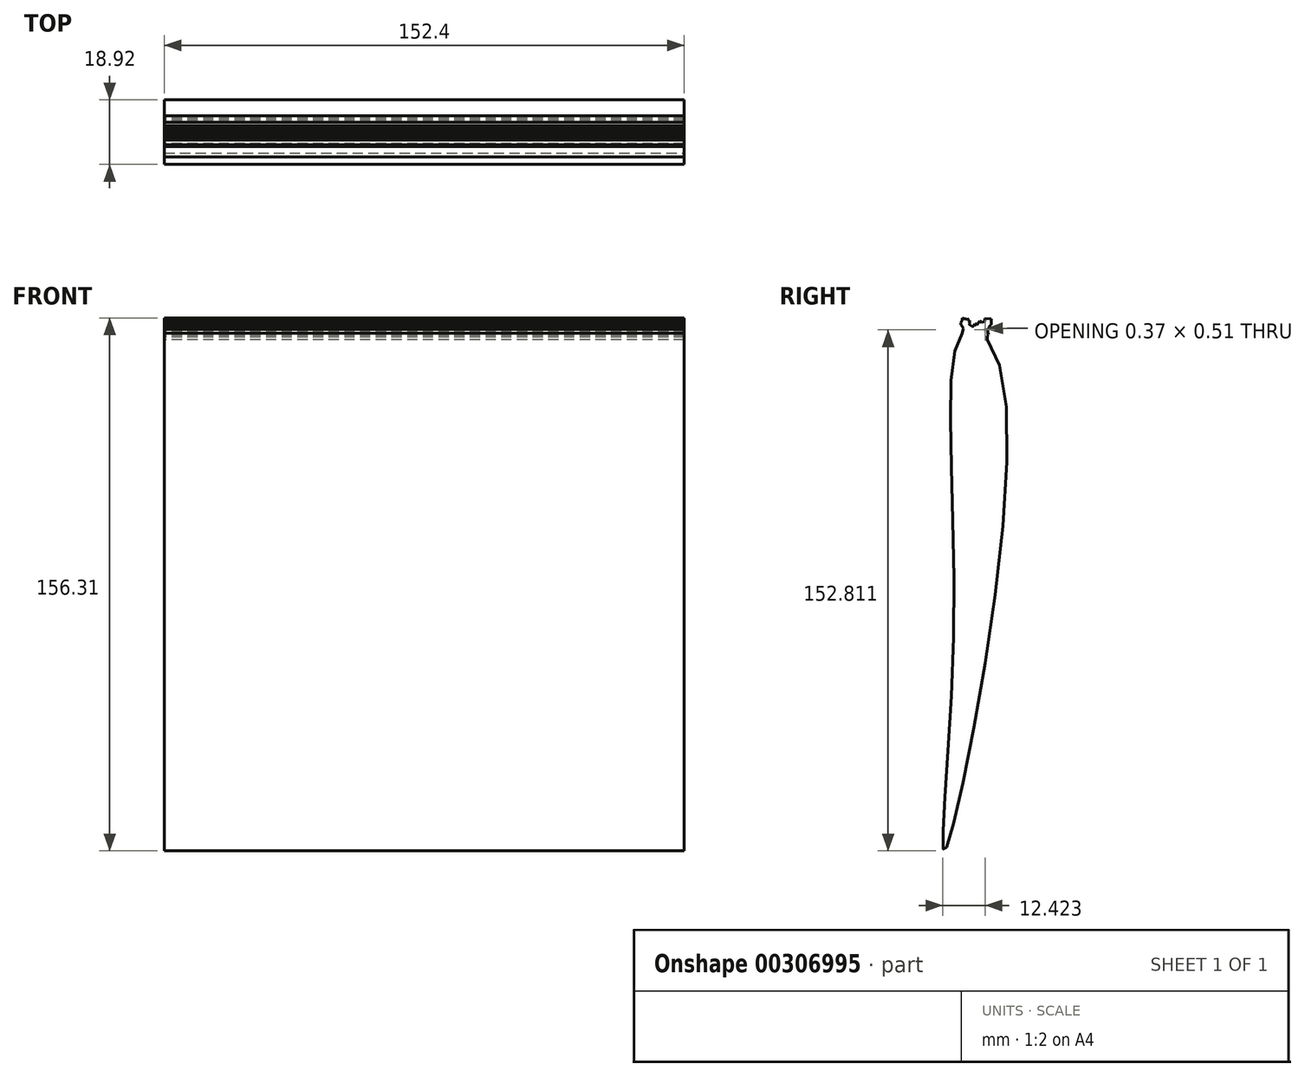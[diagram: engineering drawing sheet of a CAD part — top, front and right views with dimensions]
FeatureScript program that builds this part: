
annotation { "Feature Type Name" : "Feature", "Feature Type Description" : "" }
export const myFeature = defineFeature(function(context is Context, id is Id, definition is map)
    precondition{}
    {
        {
            var Q0;
            Q0=qCreatedBy(makeId("Right.planeOp"),FACE);
            var sketch = newSketch(context, id + "F0", { "sketchPlane" : qUnion([Q0])});
            skFitSpline(sketch, "E0", {"points": [v(3.27, 75.24) * mm, v(14.59, 61.8) * mm, v(-2.03, -76.46) * mm, v(0.33, -8.8) * mm, v(3.27, 75.24) * mm]});
            skLineSegment(sketch, "E1", {"start": v(7.38, 75.47) * mm, "end": v(9.7, 78.26) * mm});
            skLineSegment(sketch, "E2", {"start": v(9.7, 78.26) * mm, "end": v(10.74, 77.5) * mm});
            skLineSegment(sketch, "E3", {"start": v(10.74, 77.5) * mm, "end": v(8.64, 74.6) * mm});
            skLineSegment(sketch, "E4", {"start": v(8.64, 74.6) * mm, "end": v(7.38, 75.47) * mm});
            skLineSegment(sketch, "E5", {"start": v(9.7, 78.26) * mm, "end": v(10.26, 79.03) * mm});
            skPoint(sketch, "E5.endSnap0", {"position": v(10.22, 77.88) * mm});
            skLineSegment(sketch, "E6", {"start": v(10.26, 79.03) * mm, "end": v(11.26, 78.2) * mm});
            skLineSegment(sketch, "E7", {"start": v(11.26, 78.2) * mm, "end": v(10.74, 77.5) * mm});
            skLineSegment(sketch, "E8", {"start": v(4.91, 75.99) * mm, "end": v(3.97, 78.46) * mm});
            skLineSegment(sketch, "E9", {"start": v(3.97, 78.46) * mm, "end": v(2.76, 78) * mm});
            skLineSegment(sketch, "E10", {"start": v(2.76, 78) * mm, "end": v(3.7, 75.55) * mm});
            skLineSegment(sketch, "E11", {"start": v(3.7, 75.55) * mm, "end": v(4.91, 75.99) * mm});
            skLineSegment(sketch, "E12", {"start": v(9.27, 74.1) * mm, "end": v(9.32, 75.53) * mm});
            skLineSegment(sketch, "E13", {"start": v(9.32, 75.53) * mm, "end": v(9.69, 76.05) * mm});
            skLineSegment(sketch, "E14", {"start": v(9.69, 76.05) * mm, "end": v(9.68, 75.78) * mm});
            skPoint(sketch, "E14.endSnap0", {"position": v(9.5, 75.8) * mm});
            skLineSegment(sketch, "E15", {"start": v(9.68, 75.78) * mm, "end": v(9.32, 75.53) * mm});
            skLineSegment(sketch, "E16", {"start": v(9.3, 74.82) * mm, "end": v(9.9, 75.65) * mm});
            skLineSegment(sketch, "E17", {"start": v(9.9, 75.65) * mm, "end": v(9.92, 76.36) * mm});
            skLineSegment(sketch, "E18", {"start": v(9.92, 76.36) * mm, "end": v(10.37, 76.03) * mm});
            skLineSegment(sketch, "E19", {"start": v(10.37, 76.03) * mm, "end": v(9.9, 75.65) * mm});
            skLineSegment(sketch, "E20", {"start": v(10.45, 77.1) * mm, "end": v(11.3, 77.07) * mm});
            skLineSegment(sketch, "E21", {"start": v(11.3, 77.07) * mm, "end": v(10.74, 77.5) * mm});
            skLineSegment(sketch, "E22", {"start": v(11.26, 78.2) * mm, "end": v(11.31, 77.48) * mm});
            skLineSegment(sketch, "E23", {"start": v(11.31, 77.48) * mm, "end": v(10.71, 76.65) * mm});
            skLineSegment(sketch, "E24", {"start": v(10.71, 76.65) * mm, "end": v(9.92, 76.36) * mm});
            skLineSegment(sketch, "E25", {"start": v(10.71, 76.65) * mm, "end": v(10.7, 76.33) * mm});
            skLineSegment(sketch, "E26", {"start": v(10.7, 76.33) * mm, "end": v(10.37, 76.03) * mm});
            skLineSegment(sketch, "E27", {"start": v(11.31, 77.48) * mm, "end": v(10.74, 77.5) * mm});
            skLineSegment(sketch, "E28", {"start": v(10.37, 76.03) * mm, "end": v(10.34, 75.05) * mm});
            skLineSegment(sketch, "E29", {"start": v(10.34, 75.05) * mm, "end": v(9.3, 74.82) * mm});
            skLineSegment(sketch, "E30", {"start": v(11.26, 78.2) * mm, "end": v(11.28, 79) * mm});
            skLineSegment(sketch, "E31", {"start": v(11.28, 79) * mm, "end": v(10.91, 78.49) * mm});
            skLineSegment(sketch, "E32", {"start": v(10.91, 78.49) * mm, "end": v(11.28, 79) * mm});
            skLineSegment(sketch, "E33", {"start": v(11.28, 79) * mm, "end": v(10.26, 79.03) * mm});
            skLineSegment(sketch, "E34", {"start": v(10.26, 79.03) * mm, "end": v(9.44, 79.06) * mm});
            skLineSegment(sketch, "E35", {"start": v(9.44, 79.06) * mm, "end": v(9.41, 78.27) * mm});
            skLineSegment(sketch, "E36", {"start": v(9.41, 78.27) * mm, "end": v(8.46, 77.94) * mm});
            skLineSegment(sketch, "E37", {"start": v(8.46, 77.94) * mm, "end": v(7.94, 78.32) * mm});
            skLineSegment(sketch, "E38", {"start": v(7.94, 78.32) * mm, "end": v(7.9, 77.18) * mm});
            skLineSegment(sketch, "E39", {"start": v(7.9, 77.18) * mm, "end": v(7.88, 76.75) * mm});
            skLineSegment(sketch, "E40", {"start": v(7.88, 76.75) * mm, "end": v(7.16, 76.6) * mm});
            skLineSegment(sketch, "E41", {"start": v(7.16, 76.6) * mm, "end": v(7.12, 75.7) * mm});
            skLineSegment(sketch, "E42", {"start": v(7.12, 75.7) * mm, "end": v(7.38, 75.47) * mm});
            skLineSegment(sketch, "E43", {"start": v(7.94, 78.32) * mm, "end": v(7.13, 77.21) * mm});
            skLineSegment(sketch, "E44", {"start": v(7.13, 77.21) * mm, "end": v(6.53, 77.64) * mm});
            skLineSegment(sketch, "E45", {"start": v(6.53, 77.64) * mm, "end": v(6.27, 76.8) * mm});
            skLineSegment(sketch, "E46", {"start": v(6.27, 76.8) * mm, "end": v(5.55, 76.83) * mm});
            skLineSegment(sketch, "E47", {"start": v(5.55, 76.83) * mm, "end": v(5.08, 76.18) * mm});
            skLineSegment(sketch, "E48", {"start": v(5.55, 76.83) * mm, "end": v(4.92, 77.29) * mm});
            skLineSegment(sketch, "E49", {"start": v(4.92, 77.29) * mm, "end": v(4.62, 76.87) * mm});
            skLineSegment(sketch, "E50", {"start": v(4.62, 76.87) * mm, "end": v(4.64, 77.7) * mm});
            skLineSegment(sketch, "E51", {"start": v(4.64, 77.7) * mm, "end": v(4.12, 78.09) * mm});
            skLineSegment(sketch, "E52", {"start": v(4.12, 78.09) * mm, "end": v(3.97, 78.46) * mm});
            skLineSegment(sketch, "E53", {"start": v(4.64, 77.7) * mm, "end": v(4.67, 78.43) * mm});
            skLineSegment(sketch, "E54", {"start": v(4.67, 78.43) * mm, "end": v(4.12, 78.09) * mm});
            skLineSegment(sketch, "E55", {"start": v(4.67, 78.43) * mm, "end": v(5.2, 78.05) * mm});
            skLineSegment(sketch, "E56", {"start": v(5.2, 78.05) * mm, "end": v(4.64, 77.7) * mm});
            skLineSegment(sketch, "E57", {"start": v(4.67, 78.43) * mm, "end": v(4.36, 79.24) * mm});
            skLineSegment(sketch, "E58", {"start": v(4.36, 79.24) * mm, "end": v(3.97, 78.46) * mm});
            skLineSegment(sketch, "E59", {"start": v(3.97, 78.46) * mm, "end": v(3.39, 78.88) * mm});
            skPoint(sketch, "E59.endSnap0", {"position": v(3.37, 78.23) * mm});
            skLineSegment(sketch, "E60", {"start": v(3.39, 78.88) * mm, "end": v(2.76, 78) * mm});
            skLineSegment(sketch, "E61", {"start": v(2.76, 78) * mm, "end": v(2.8, 79.3) * mm});
            skLineSegment(sketch, "E62", {"start": v(2.8, 79.3) * mm, "end": v(4.17, 78.85) * mm});
            skLineSegment(sketch, "E63", {"start": v(4.17, 78.85) * mm, "end": v(4.36, 79.24) * mm});
            skLineSegment(sketch, "E64", {"start": v(2.78, 78.5) * mm, "end": v(2.26, 77.8) * mm});
            skLineSegment(sketch, "E65", {"start": v(2.26, 77.8) * mm, "end": v(3.3, 76.6) * mm});
            skLineSegment(sketch, "E66", {"start": v(3.3, 76.6) * mm, "end": v(2.62, 76.94) * mm});
            skLineSegment(sketch, "E67", {"start": v(2.62, 76.94) * mm, "end": v(2.45, 77.37) * mm});
            skLineSegment(sketch, "E68", {"start": v(2.45, 77.37) * mm, "end": v(2.26, 77.8) * mm});
            skLineSegment(sketch, "E69", {"start": v(3.7, 75.55) * mm, "end": v(3.27, 75.24) * mm});
            skLineSegment(sketch, "E70", {"start": v(3.27, 75.24) * mm, "end": v(3.02, 75.89) * mm});
            skLineSegment(sketch, "E71", {"start": v(3.02, 75.89) * mm, "end": v(3.38, 76.5) * mm});
            skLineSegment(sketch, "E72", {"start": v(3.38, 76.5) * mm, "end": v(2.62, 76.94) * mm});
            skLineSegment(sketch, "E73", {"start": v(2.62, 76.94) * mm, "end": v(3.2, 76.2) * mm});
            skLineSegment(sketch, "E74", {"start": v(10.34, 75.05) * mm, "end": v(10.5, 74.37) * mm});
            skLineSegment(sketch, "E75", {"start": v(10.5, 74.37) * mm, "end": v(10, 74.2) * mm});
            skLineSegment(sketch, "E76", {"start": v(10, 74.2) * mm, "end": v(10.2, 73.6) * mm});
            skLineSegment(sketch, "E77", {"start": v(10.2, 73.6) * mm, "end": v(10.18, 72.93) * mm});
            skLineSegment(sketch, "E78", {"start": v(10.18, 72.93) * mm, "end": v(9.27, 74.1) * mm});
            skLineSegment(sketch, "E79", {"start": v(3.02, 75.89) * mm, "end": v(2.75, 74.74) * mm});
            skLineSegment(sketch, "E80", {"start": v(2.75, 74.74) * mm, "end": v(3.27, 75.24) * mm});
            skLineSegment(sketch, "E81", {"start": v(4.64, 77.7) * mm, "end": v(4.92, 77.29) * mm});
            skLineSegment(sketch, "E82.0", {"start": v(3.02, 75.89) * mm, "end": v(9.9, 75.65) * mm, "construction": true});
            skLineSegment(sketch, "E83.0", {"start": v(2.45, 77.37) * mm, "end": v(11.3, 77.07) * mm, "construction": true});
            skLineSegment(sketch, "E84.0", {"start": v(2.62, 76.94) * mm, "end": v(5.55, 76.83) * mm, "construction": true});
            skLineSegment(sketch, "E85.0", {"start": v(3.3, 76.6) * mm, "end": v(10.7, 76.33) * mm, "construction": true});
            skLineSegment(sketch, "E86.0", {"start": v(2.26, 77.8) * mm, "end": v(11.31, 77.48) * mm, "construction": true});
            skLineSegment(sketch, "E87.0", {"start": v(2.8, 79.3) * mm, "end": v(11.28, 79) * mm, "construction": true});
            skLineSegment(sketch, "E88.0", {"start": v(2.78, 78.5) * mm, "end": v(11.26, 78.2) * mm, "construction": true});
            skLineSegment(sketch, "E89.0", {"start": v(4.12, 78.09) * mm, "end": v(10.22, 77.88) * mm, "construction": true});
            skLineSegment(sketch, "E90.0", {"start": v(9.5, 75.8) * mm, "end": v(9.68, 75.78) * mm, "construction": true});
            skLineSegment(sketch, "E91.0", {"start": v(7.13, 77.21) * mm, "end": v(7.9, 77.18) * mm, "construction": true});
            skLineSegment(sketch, "E92.0", {"start": v(7.88, 76.75) * mm, "end": v(10.71, 76.65) * mm, "construction": true});
            skLineSegment(sketch, "E93.0", {"start": v(3.3, 76.6) * mm, "end": v(3.39, 78.88) * mm, "construction": true});
            skLineSegment(sketch, "E94.0", {"start": v(10.71, 76.65) * mm, "end": v(10.74, 77.5) * mm, "construction": true});
            skLineSegment(sketch, "E95.0", {"start": v(2.76, 78) * mm, "end": v(2.78, 78.5) * mm, "construction": true});
            skLineSegment(sketch, "E96.0", {"start": v(10.22, 77.88) * mm, "end": v(10.26, 79.03) * mm, "construction": true});
            skLineSegment(sketch, "E97.0", {"start": v(9.3, 74.82) * mm, "end": v(9.44, 79.06) * mm, "construction": true});
            skLineSegment(sketch, "E98.0", {"start": v(11.3, 77.07) * mm, "end": v(11.31, 77.48) * mm, "construction": true});
            skSolve(sketch);
        }
        {
            var Q0;
            Q0=qSketchRegion(id+"F0",true);
            var Q1;
            Q1=makeQuery(id+"F0.imprint","IMPRINT",FACE,{"disambiguationData":[TD([[makeQuery(id+"F0.imprint","IMPRINT",EDGE,{"derivedFrom":sQuery(id+"F0.wireOp",EDGE,"E1")}),1.0]])]});
            var Q2;
            {var subQ3=sQuery(id+"F0.wireOp",EDGE,"E1");Q2=makeQuery(id+"F0.imprint","IMPRINT",FACE,{"disambiguationData":[TD([[makeQuery(id+"F0.imprint","IMPRINT",EDGE,{"derivedFrom":subQ3}),-1.0]])]});}
            var Q3;
            {var subQ0=sQuery(id+"F0.wireOp",EDGE,"E29");Q3=makeQuery(id+"F0.imprint","IMPRINT",FACE,{"disambiguationData":[TD([[makeQuery(id+"F0.imprint","IMPRINT",EDGE,{"derivedFrom":subQ0}),1.0]])]});}
            var Q4;
            {var subQ0=sQuery(id+"F0.wireOp",EDGE,"E78");var subQ1=sQuery(id+"F0.wireOp",EDGE,"E12");var subQ2=makeQuery(id+"F0.imprint","INTERSECT",VERTEX,{"derivedFrom":[subQ1,subQ0]});Q4=makeQuery(id+"F0.imprint","IMPRINT",FACE,{"disambiguationData":[TD([[makeQuery(id+"F0.imprint","IMPRINT",EDGE,{"disambiguationData":[TD([[subQ2,1.0]])],"derivedFrom":subQ0}),1.0]])]});}
            var Q5;
            {var subQ2=sQuery(id+"F0.wireOp",EDGE,"E8");Q5=makeQuery(id+"F0.imprint","IMPRINT",FACE,{"disambiguationData":[TD([[makeQuery(id+"F0.imprint","IMPRINT",EDGE,{"derivedFrom":subQ2}),-1.0]])]});}
            var Q6;
            {var subQ0=sQuery(id+"F0.wireOp",EDGE,"E11");Q6=makeQuery(id+"F0.imprint","IMPRINT",FACE,{"disambiguationData":[TD([[makeQuery(id+"F0.imprint","IMPRINT",EDGE,{"derivedFrom":subQ0}),1.0]])]});}
            var Q7;
            {var subQ0=sQuery(id+"F0.wireOp",EDGE,"E4");Q7=makeQuery(id+"F0.imprint","IMPRINT",FACE,{"disambiguationData":[TD([[makeQuery(id+"F0.imprint","IMPRINT",EDGE,{"derivedFrom":subQ0}),-1.0]])]});}
            var Q8;
            {var subQ0=sQuery(id+"F0.wireOp",EDGE,"E78");var subQ1=sQuery(id+"F0.wireOp",EDGE,"E0");var subQ3=makeQuery(id+"F0.imprint","INTERSECT",VERTEX,{"derivedFrom":[subQ1,subQ0]});Q8=makeQuery(id+"F0.imprint","IMPRINT",FACE,{"disambiguationData":[TD([[makeQuery(id+"F0.imprint","IMPRINT",EDGE,{"disambiguationData":[TD([[subQ3,-1.0]])],"derivedFrom":subQ1}),-1.0]])]});}
            var Q9;
            {var subQ6=sQuery(id+"F0.wireOp",EDGE,"E8");Q9=makeQuery(id+"F0.imprint","IMPRINT",FACE,{"disambiguationData":[TD([[makeQuery(id+"F0.imprint","IMPRINT",EDGE,{"derivedFrom":subQ6}),1.0]])]});}
            var Q10;
            Q10=makeQuery(id+"F0.imprint","IMPRINT",FACE,{"disambiguationData":[TD([[makeQuery(id+"F0.imprint","IMPRINT",EDGE,{"derivedFrom":sQuery(id+"F0.wireOp",EDGE,"E58")}),-1.0]])]});
            var Q11;
            {var subQ0=sQuery(id+"F0.wireOp",EDGE,"E69");Q11=makeQuery(id+"F0.imprint","IMPRINT",FACE,{"disambiguationData":[TD([[makeQuery(id+"F0.imprint","IMPRINT",EDGE,{"derivedFrom":subQ0}),-1.0]])]});}
            var Q12;
            {var subQ1=sQuery(id+"F0.wireOp",EDGE,"E70");Q12=makeQuery(id+"F0.imprint","IMPRINT",FACE,{"disambiguationData":[TD([[makeQuery(id+"F0.imprint","IMPRINT",EDGE,{"derivedFrom":subQ1}),1.0]])]});}
            var Q13;
            {var subQ0=sQuery(id+"F0.wireOp",EDGE,"E80");Q13=makeQuery(id+"F0.imprint","IMPRINT",FACE,{"disambiguationData":[TD([[makeQuery(id+"F0.imprint","IMPRINT",EDGE,{"derivedFrom":subQ0}),1.0]])]});}
            var Q14;
            {var subQ5=sQuery(id+"F0.wireOp",EDGE,"E64");Q14=makeQuery(id+"F0.imprint","IMPRINT",FACE,{"disambiguationData":[TD([[makeQuery(id+"F0.imprint","IMPRINT",EDGE,{"derivedFrom":subQ5}),1.0]])]});}
            var Q15;
            {var subQ1=sQuery(id+"F0.wireOp",EDGE,"E70");Q15=makeQuery(id+"F0.imprint","IMPRINT",FACE,{"disambiguationData":[TD([[makeQuery(id+"F0.imprint","IMPRINT",EDGE,{"derivedFrom":subQ1}),-1.0]])]});}
            var Q16;
            {var subQ0=sQuery(id+"F0.wireOp",EDGE,"E67");Q16=makeQuery(id+"F0.imprint","IMPRINT",FACE,{"disambiguationData":[TD([[makeQuery(id+"F0.imprint","IMPRINT",EDGE,{"derivedFrom":subQ0}),-1.0]])]});}
            var Q17;
            {var subQ0=sQuery(id+"F0.wireOp",EDGE,"E72");var subQ1=sQuery(id+"F0.wireOp",EDGE,"E10");var subQ2=makeQuery(id+"F0.imprint","INTERSECT",VERTEX,{"derivedFrom":[subQ1,subQ0]});Q17=makeQuery(id+"F0.imprint","IMPRINT",FACE,{"disambiguationData":[TD([[makeQuery(id+"F0.imprint","IMPRINT",EDGE,{"disambiguationData":[TD([[subQ2,-1.0]])],"derivedFrom":subQ1}),1.0]])]});}
            var Q18;
            Q18=makeQuery(id+"F0.imprint","IMPRINT",FACE,{"disambiguationData":[TD([[makeQuery(id+"F0.imprint","IMPRINT",EDGE,{"derivedFrom":sQuery(id+"F0.wireOp",EDGE,"E9")}),-1.0]])]});
            var Q19;
            Q19=makeQuery(id+"F0.imprint","IMPRINT",FACE,{"disambiguationData":[TD([[makeQuery(id+"F0.imprint","IMPRINT",EDGE,{"derivedFrom":sQuery(id+"F0.wireOp",EDGE,"E17")}),-1.0]])]});
            var Q20;
            {var subQ0=sQuery(id+"F0.wireOp",EDGE,"E65");var subQ1=sQuery(id+"F0.wireOp",EDGE,"E10");var subQ2=makeQuery(id+"F0.imprint","INTERSECT",VERTEX,{"derivedFrom":[subQ1,subQ0]});Q20=makeQuery(id+"F0.imprint","IMPRINT",FACE,{"disambiguationData":[TD([[makeQuery(id+"F0.imprint","IMPRINT",EDGE,{"disambiguationData":[TD([[subQ2,-1.0]])],"derivedFrom":subQ1}),1.0]])]});}
            var Q21;
            Q21=makeQuery(id+"F0.imprint","IMPRINT",FACE,{"disambiguationData":[TD([[makeQuery(id+"F0.imprint","IMPRINT",EDGE,{"derivedFrom":sQuery(id+"F0.wireOp",EDGE,"E18")}),1.0]])]});
            var Q22;
            Q22=makeQuery(id+"F0.imprint","IMPRINT",FACE,{"disambiguationData":[TD([[makeQuery(id+"F0.imprint","IMPRINT",EDGE,{"derivedFrom":sQuery(id+"F0.wireOp",EDGE,"E49")}),-1.0]])]});
            var Q23;
            {var subQ2=sQuery(id+"F0.wireOp",EDGE,"E32");Q23=makeQuery(id+"F0.imprint","IMPRINT",FACE,{"disambiguationData":[TD([[makeQuery(id+"F0.imprint","IMPRINT",EDGE,{"derivedFrom":subQ2}),1.0]])]});}
            var Q24;
            {var subQ0=sQuery(id+"F0.wireOp",EDGE,"E66");var subQ1=sQuery(id+"F0.wireOp",EDGE,"E10");var subQ2=makeQuery(id+"F0.imprint","INTERSECT",VERTEX,{"derivedFrom":[subQ1,subQ0]});Q24=makeQuery(id+"F0.imprint","IMPRINT",FACE,{"disambiguationData":[TD([[makeQuery(id+"F0.imprint","IMPRINT",EDGE,{"disambiguationData":[TD([[subQ2,-1.0]])],"derivedFrom":subQ1}),-1.0]])]});}
            var Q25;
            Q25=makeQuery(id+"F0.imprint","IMPRINT",FACE,{"disambiguationData":[TD([[makeQuery(id+"F0.imprint","IMPRINT",EDGE,{"derivedFrom":sQuery(id+"F0.wireOp",EDGE,"E2")}),1.0]])]});
            var Q26;
            {var subQ5=sQuery(id+"F0.wireOp",EDGE,"E73");Q26=makeQuery(id+"F0.imprint","IMPRINT",FACE,{"disambiguationData":[TD([[makeQuery(id+"F0.imprint","IMPRINT",EDGE,{"derivedFrom":subQ5}),1.0]])]});}
            var Q27;
            {var subQ1=sQuery(id+"F0.wireOp",EDGE,"E14");Q27=makeQuery(id+"F0.imprint","IMPRINT",FACE,{"disambiguationData":[TD([[makeQuery(id+"F0.imprint","IMPRINT",EDGE,{"derivedFrom":subQ1}),1.0]])]});}
            var Q28;
            Q28=makeQuery(id+"F0.imprint","IMPRINT",FACE,{"disambiguationData":[TD([[makeQuery(id+"F0.imprint","IMPRINT",EDGE,{"derivedFrom":sQuery(id+"F0.wireOp",EDGE,"E16")}),-1.0]])]});
            var Q29;
            {var subQ0=sQuery(id+"F0.wireOp",EDGE,"E24");Q29=makeQuery(id+"F0.imprint","IMPRINT",FACE,{"disambiguationData":[TD([[makeQuery(id+"F0.imprint","IMPRINT",EDGE,{"derivedFrom":subQ0}),-1.0]])]});}
            var Q30;
            Q30=makeQuery(id+"F0.imprint","IMPRINT",FACE,{"disambiguationData":[TD([[makeQuery(id+"F0.imprint","IMPRINT",EDGE,{"derivedFrom":sQuery(id+"F0.wireOp",EDGE,"E13")}),-1.0]])]});
            var Q31;
            {var subQ0=sQuery(id+"F0.wireOp",EDGE,"E21");var subQ1=sQuery(id+"F0.wireOp",EDGE,"E20");var subQ2=makeQuery(id+"F0.imprint","INTERSECT",VERTEX,{"derivedFrom":[subQ1,subQ0]});Q31=makeQuery(id+"F0.imprint","IMPRINT",FACE,{"disambiguationData":[TD([[makeQuery(id+"F0.imprint","IMPRINT",EDGE,{"disambiguationData":[TD([[subQ2,1.0]])],"derivedFrom":subQ1}),1.0]])]});}
            var Q32;
            Q32=makeQuery(id+"F0.imprint","IMPRINT",FACE,{"disambiguationData":[TD([[makeQuery(id+"F0.imprint","IMPRINT",EDGE,{"derivedFrom":sQuery(id+"F0.wireOp",EDGE,"E53")}),-1.0]])]});
            var Q33;
            {var subQ0=sQuery(id+"F0.wireOp",EDGE,"E30");Q33=makeQuery(id+"F0.imprint","IMPRINT",FACE,{"disambiguationData":[TD([[makeQuery(id+"F0.imprint","IMPRINT",EDGE,{"derivedFrom":subQ0}),1.0]])]});}
            var Q34;
            Q34=makeQuery(id+"F0.imprint","IMPRINT",FACE,{"disambiguationData":[TD([[makeQuery(id+"F0.imprint","IMPRINT",EDGE,{"derivedFrom":sQuery(id+"F0.wireOp",EDGE,"E7")}),1.0]])]});
            var Q35;
            Q35=makeQuery(id+"F0.imprint","IMPRINT",FACE,{"disambiguationData":[TD([[makeQuery(id+"F0.imprint","IMPRINT",EDGE,{"derivedFrom":sQuery(id+"F0.wireOp",EDGE,"E51")}),-1.0]])]});
            var Q36;
            Q36=makeQuery(id+"F0.imprint","IMPRINT",FACE,{"disambiguationData":[TD([[makeQuery(id+"F0.imprint","IMPRINT",EDGE,{"derivedFrom":sQuery(id+"F0.wireOp",EDGE,"E52")}),-1.0]])]});
            var Q37;
            {var subQ1=sQuery(id+"F0.wireOp",EDGE,"E3");var subQ3=sQuery(id+"F0.wireOp",EDGE,"E20");var subQ4=makeQuery(id+"F0.imprint","INTERSECT",VERTEX,{"derivedFrom":[subQ1,subQ3]});Q37=makeQuery(id+"F0.imprint","IMPRINT",FACE,{"disambiguationData":[TD([[makeQuery(id+"F0.imprint","IMPRINT",EDGE,{"disambiguationData":[TD([[subQ4,-1.0]])],"derivedFrom":subQ3}),1.0]])]});}
            var Q38;
            {var subQ0=sQuery(id+"F0.wireOp",EDGE,"E27");Q38=makeQuery(id+"F0.imprint","IMPRINT",FACE,{"disambiguationData":[TD([[makeQuery(id+"F0.imprint","IMPRINT",EDGE,{"derivedFrom":subQ0}),1.0]])]});}
            var Q39;
            {var subQ4=sQuery(id+"F0.wireOp",EDGE,"E4");Q39=makeQuery(id+"F0.imprint","IMPRINT",FACE,{"disambiguationData":[TD([[makeQuery(id+"F0.imprint","IMPRINT",EDGE,{"derivedFrom":subQ4}),1.0]])]});}
            extrude(context, id + "F1", {"entities" : qUnion([Q0, Q1, Q2, Q3, Q4, Q5, Q6, Q7, Q8, Q9, Q10, Q11, Q12, Q13, Q14, Q15, Q16, Q17, Q18, Q19, Q20, Q21, Q22, Q23, Q24, Q25, Q26, Q27, Q28, Q29, Q30, Q31, Q32, Q33, Q34, Q35, Q36, Q37, Q38, Q39]), "depth" : 76.2 * mm, "hasSecondDirection" : true, "secondDirectionOppositeDirection" : true, "secondDirectionDepth" : 76.2 * mm});
        }
    });
